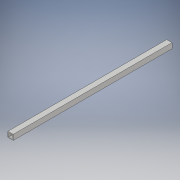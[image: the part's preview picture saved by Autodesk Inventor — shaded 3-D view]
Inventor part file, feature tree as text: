
AUTODESK INVENTOR PART (.ipt)
format: ipt  version: 2018 (Build 220112000, 112)  size: 97,792 bytes
history: native  units: in
note: dims shown in document units (in); Inventor stores cm internally (conversion verified against a paired STEP export)
features: extrude x1, sketch x1
ambient origin geometry x8: Origin, YZ Plane, XZ Plane, XY Plane, X Axis, Y Axis, Z Axis, Center Point
bodies: Solid1 (feature_tree)
feature tree (2):
  extrude  "Extrusion1"  Depth=1.0in
  sketch  "Sketch1"  dims[d0=1.0in d1=1.0in d2=0.125in d3=30.0in d4=0.0in]
